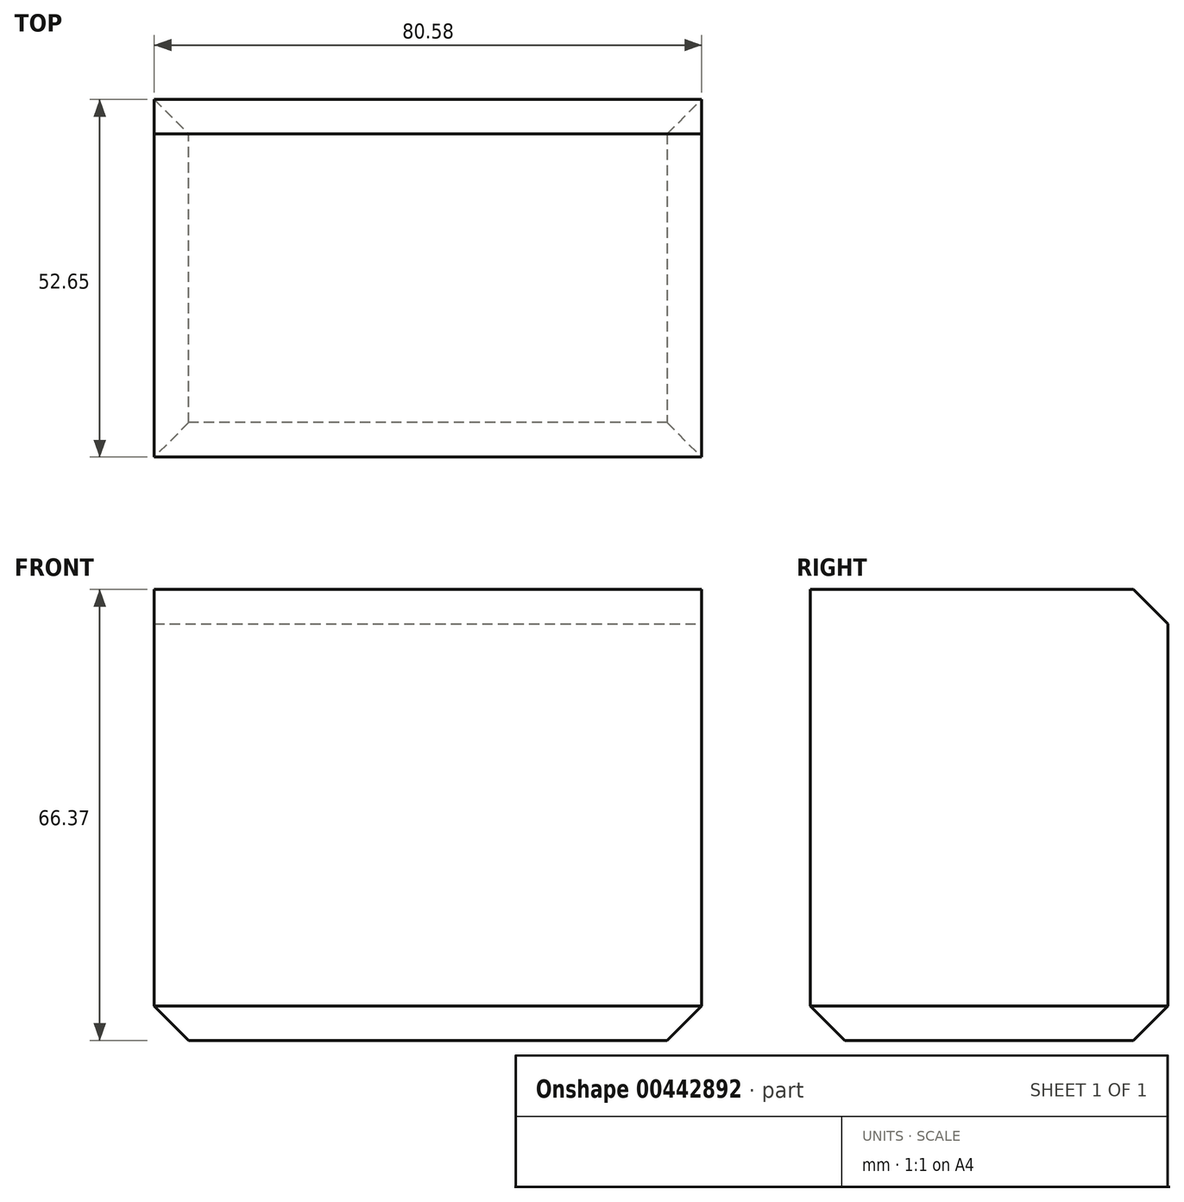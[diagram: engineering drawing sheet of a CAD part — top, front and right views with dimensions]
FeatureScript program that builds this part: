
annotation { "Feature Type Name" : "Feature", "Feature Type Description" : "" }
export const myFeature = defineFeature(function(context is Context, id is Id, definition is map)
    precondition{}
    {
        {
            var Q0;
            Q0=qCreatedBy(makeId("Top.planeOp"),FACE);
            var sketch = newSketch(context, id + "F0", { "sketchPlane" : qUnion([Q0])});
            skLineSegment(sketch, "E0.bottom", {"start": v(-30.4, 52.65) * mm, "end": v(50.18, 52.65) * mm});
            skLineSegment(sketch, "E0.top", {"start": v(-30.4, 0) * mm, "end": v(50.18, 0) * mm});
            skLineSegment(sketch, "E0.left", {"start": v(-30.4, 52.65) * mm, "end": v(-30.4, 0) * mm});
            skLineSegment(sketch, "E0.right", {"start": v(50.18, 52.65) * mm, "end": v(50.18, 0) * mm});
            skSolve(sketch);
        }
        {
            var Q0;
            Q0=makeQuery(id+"F0.imprint","IMPRINT",FACE,{"disambiguationData":[TD([[makeQuery(id+"F0.imprint","IMPRINT",EDGE,{"derivedFrom":sQuery(id+"F0.wireOp",EDGE,"E0.bottom")}),-1.0]])]});
            extrude(context, id + "F1", {"entities" : qUnion([Q0]), "depth" : 66.37 * mm});
        }
        {
            var Q0;
            Q0=makeQuery(id+"F1.opExtrude","CAP_EDGE",EDGE,{"disambiguationData":[OSD([sQuery(id+"F0.wireOp",EDGE,"E0.bottom")])],"isStart":false});
            chamfer(context, id + "F2", {"entities" : qUnion([Q0]), "width" : 5.08 * mm, "tangentPropagation" : true});
        }
        {
            var Q0;
            Q0=makeQuery(id+"F1.opExtrude","CAP_FACE",FACE,{"disambiguationData":[OSD([sQuery(id+"F0.wireOp",EDGE,"E0.bottom"),sQuery(id+"F0.wireOp",EDGE,"E0.top"),sQuery(id+"F0.wireOp",EDGE,"E0.left"),sQuery(id+"F0.wireOp",EDGE,"E0.right")])],"isStart":true});
            chamfer(context, id + "F3", {"entities" : qUnion([Q0]), "width" : 5.08 * mm, "tangentPropagation" : true});
        }
    });
